FCSTD DOCUMENT  (FreeCAD 1.0R39109 (Git))
Label: Master Document
License: All rights reserved
LicenseURL: http://en.wikipedia.org/wiki/All_rights_reserved
objects: Spreadsheet::Sheet×1

FEATURE [Spreadsheet::Sheet] Spreadsheet  label="Monitor Chassis Parameters"
  cells = A1='Parameter Name; B1='Value; C1='Notes; A2='GSWallHalfLength; B2(GSWallHalfLength)==B77; C2='Does not include outer radius portion of the wall, only the rectangular part; A3='GSBottomWallHeight; B3(GSBottomWallHeight)==B108 + B127 + B11; A4='GSWallWidth; B4(GSWallWidth)=123; A5='GSBaseFloorBeamWidth; B5(GSBaseFloorBeamWidth)==B49 * 3; C5='Is relelative to the size of the screw hole size; A6='GSBaseBodyThickness; B6(GSBaseBodyThickness)=3; A7='GSCamWallThickness; B7(GSCamWallThickness)=4; A8='GSThinWallThickness; B8(GSThinWallThickness)=3; A9='GSCamWallClickIndent; B9(GSCamWallClickIndent)=1; A10='GSCamWallClickLength; B10(GSCamWallClickLength)=6; A11='GSCamWallFullClickStructureHeight; B11(GSCamWallFullClickStructureHeight)=20; A14='GSCamBoardHeight; B14(GSCamBoardHeight)=38; A15='GSCamBoardWidth; B15(GSCamBoardWidth)=38; A16='GSCamBoardMountingHoleDiameter; B16(GSCamBoardMountingHoleDiameter)==B60; A17='GSCamPlateThickness; B17(GSCamPlateThickness)=4; A18='GSCamMountingHoleOffset; B18(GSCamMountingHoleOffset)=4; A19='GSCamMountingHoleThickness; B19(GSCamMountingHoleThickness)=2; A20='GSCamMountingHoleHeight; B20(GSCamMountingHoleHeight)=7; A21='GSCamAxisHoleDiameter; B21(GSCamAxisHoleDiameter)==B61; C21='M4 uses a 4.5 mm hole; A22='GSCamAxisWidth; B22(GSCamAxisWidth)=22; A23='GSCamMountingIndentInnerDiameter; B23(GSCamMountingIndentInnerDiameter)=5; C23='TBD - Not a good name?; A24='GSCamMountingHoleDiameter; B24(GSCamMountingHoleDiameter)=2.5; A25='GSCamGimbalDepth; B25(GSCamGimbalDepth)=20; A26='GSCam1ZAxisSetback; B26(GSCam1ZAxisSetback)=15; C26='The camera will be mounted further back than for camera 2, away from the lens to help the tilt ability; A27='GSCam2ZAxisSetback; B27(GSCam2ZAxisSetback)=15; C27='The camera will be mounted back, away from the lens to help the tilt ability; A28='GSCamGimbalLighteningSlotOffsetFromCenter; B28(GSCamGimbalLighteningSlotOffsetFromCenter)=12; A29='GSCamGimbalInnerLength; B29(GSCamGimbalInnerLength)=58; A30='GSCam1GimbalHoleHeight; B30(GSCam1GimbalHoleHeight)=50; C30='The camera will sit higher to allow it to more easily tilt downward at the teed-up ball; A31='GSCam2GimbalHoleHeight; B31(GSCam2GimbalHoleHeight)=35; A33='GSIMakerCamBoardHeight; B33(GSIMakerCamBoardHeight)=39; C33='These next parameters are for the Innomaker CAM-IMX296 global shutter camera; A34='GSIMakerCamBoardWidth; B34(GSIMakerCamBoardWidth)=39; A35='GSIMakerCamBoardMountingHoleDiameter; B35(GSIMakerCamBoardMountingHoleDiameter)==GSM2BoltHoleDiameter; A36='GSIMakerCamMountingHoleOffset; B36(GSIMakerCamMountingHoleOffset)=2.5; C36='We want a 34mm distance between the hole centers; A37='GSIMakerCamMountingHoleThickness; B37(GSIMakerCamMountingHoleThickness)=2; A38='GSIMakerCamMountingHoleHeight; B38(GSIMakerCamMountingHoleHeight)=4; C38='Want short enough to abe able to use commonly-found M2x12 bolts; A39='GSIMakerCamMountingRiserDiameter; B39(GSIMakerCamMountingRiserDiameter)=4; A41='GSIMakerCam1GimbalHoleHeight; B41(GSIMakerCam1GimbalHoleHeight)=40; C41='The camera will sit a higher to allow it to more easily tilt downward at the teed-up ball.  This is less important if we're using a shorter M12 lens; A42='GSIMakerCam2GimbalHoleHeight; B42(GSIMakerCam2GimbalHoleHeight)=40; A44='GSImakerCamPinCutoutWidth; B44(GSImakerCamPinCutoutWidth)=4; A45='GSImakerCamPinCutoutSideOffset; B45(GSImakerCamPinCutoutSideOffset)=5; A46='GSImakerCamPinCutoutTopOffset; B46(GSImakerCamPinCutoutTopOffset)=6.5; A48='GSCamM4NutHexagonDiameter; B48(GSCamM4NutHexagonDiameter)=8.4; A49='GSCamM4ScrewHoleDiameter; B49(GSCamM4ScrewHoleDiameter)=3.3; A50='GSM4CountersunkScrewHoleDiameter; B50(GSM4CountersunkScrewHoleDiameter)=4.5; A51='GSCamM4NutDepth; B51(GSCamM4SNutDepth)=4; A52='GSCamM3NutDepth; B52(GSCamM3NutDepth)=3.5; A53='GSCamM5NutHexagonDiameter; B53(GSCamM5NutHexagonDiameter)=9.5; A54='GSCamM3NutHexagonDiameter; B54(GSCamM3NutHexagonDiameter)=6.6; A55='GSCamM5ScrewHoleDiameter; B55(GSCamM5ScrewHoleDiameter)=5.5; A56='GSCamM5NutDepth; B56(GSCamM5NutDepth)=4; A57='GSLEDPowerRiserHeight; B57(GSLEDPowerRiserHeight)=7; A58='GSM3BoltHoleDiameter; B58(GSM3BoltHoleDiameter)=3.4; A59='GSM2BoltHoleDiameter; B59(GSM2BoltHoleDiameter)=2.4; A60='GSM25BoltHoleDiameter; B60(GSM25BoltHoleDiameter)=2.9; A61='GSM4BoltHoleDiameter; B61(GSM4BoltHoleDiameter)=4.5; A62='GSM4BoltHeadIndentDiameter; B62(GSM4BoltHeadIndentDiameter)=7.5; A63='GSM4BoltCountersinkDiameter; B63(GSM4BoltCountersinkDiameter)=8; A64='GSM3BoltCountersinkDiameter; B64(GSM3BoltCountersinkDiameter)=5.3; A65='GSM2BoltCountersinkDiameter; B65(GSM2BoltCountersinkDiameter)=3.5; A66='GSM25ThreaadedInsertDiameter; B66(GSM25ThreaadedInsertDiameter)=3.4; A67='GSM3ThreaadedInsertDiameter; B67(GSM3ThreaadedInsertDiameter)=4.25; A69='GSM2TappingScrewHoleDiameter; B69(GSM2TappingScrewHoleDiameter)=1.71; A70='GSM2_5TappingScrewHoleDiameter; B70(GSM2_5TappingScrewHoleDiameter)=2.05; A71='GSM3TappingScrewHoleDiameter; B71(GSM3TappingScrewHoleDiameter)=2.4; A72='GSM4TappingScrewHoleDiameter; B72(GSM4TappingScrewHoleDiameter)=3.4; A74='GSMonitorFloorPowerBayLength; B74(GSMonitorFloorPowerBayLength)=155; A76='GSMonitorFloorWidth_PiSide; B76(GSMonitorFloorWidth_PiSide)==B4 - 2 * B8; A77='GSMonitorFloorLength_PiSide; B77(GSMonitorFloorLength_PiSide)=170; A78='GSMonitorCameraBayLength; B78(GSMonitorCameraBayLength)=130; C78='TBD - May not use.  Instead, just have a single right- and left- number so that the viewports are the same?; F78='Total Inner Length; G78==B78 + B83 + B84 + B94; A79='GSMonitorStrobeBayLength; B79(GSMonitorStrobeBayLength)=130; C79='TBD - Not used; A80='GSMonitorViewPortLengthRight; B80(GSMonitorViewPortLengthRight)=100; A81='GSMonitorViewPortLengthLeft; B81(GSMonitorViewPortLengthLeft)=50; A83='GSMonitorPiBayLength; B83(GSMonitorPiBayLength)=100; A84='GSMonitorExtraBayLength; B84(GSMonitorExtraBayLength)=10; A85='GSMonitorFloorThickness; B85(GSMonitorFloorThickness)=4; A86='GSMonitorFloorPiSideLengthShare; B86(GSMonitorFloorPiSideLengthShare)=30; C86='This amount of the Pi-side is moved to the Power side to share the overall length to fit on printer; A87='GSMonitorFloorJointOverlap; B87(GSMonitorFloorJointOverlap)=14; A88='GSMonitorFloorPiEndOffset; B88(GSMonitorFloorPiEndOffset)=32; C88='Offset from end of floor rectangle (not rounded part) to nearest Pi board mounting hole; A89='GSMonitorFloorPiNearSideOffset; B89(GSMonitorFloorPiNearSideOffset)=51; C89='Offset from camera side of inner wall to the Pi 5 mounting screw; A90='GSMonitorFloorMountHoleSideOffset; B90(GSMonitorFloorMountHoleSideOffset)=8; C90='From inner side to the hole that the floor will be screwed into; A91='GSMonitorFloorMountHoleSideOffsetForWall; B91(GSMonitorFloorMountHoleSideOffsetForWall)==B90 - 1; C91='TBD - Fix so that a separate value here is not needed.  Needed because wall measures the side offset from the lip, not the  same place the Floor does.; A92='GSM5ScrewHoleDiameter; B92(GSM5ScrewHoleDiameter)=3.3; A93='GSMonitorFloorMountHoleEdgeOffset; B93(GSMonitorFloorMountHoleEdgeOffset)=8; C93='From edge (e.g., from the side or the middle of the floors) back to the screw that will mount to the wall; A94='GSMonitorFloorPowerBayLength; B94=150; A95='GSMonitorFloorMountingScrewDiameter; B95(GSMonitorFloorMountingScrewDiameter)=2.5; C95='2.4 is nominal, but that was a little tight in PLA; A96='GSMonitorFloorRibMinimumWidth; B96(GSMonitorFloorRibMinimumWidth)=10; A97='GSMonitorFloorMountingScrewDepth; B97(GSMonitorFloorMountingScrewDepth)=6; A98='GSMonitorWallTensionReliefCutWidth; B98(GSMonitorWallTensionReliefCutWidth)=0.5; A99='GSMonitorWallHalfConnectionBoltDiameter; +591 more cells
